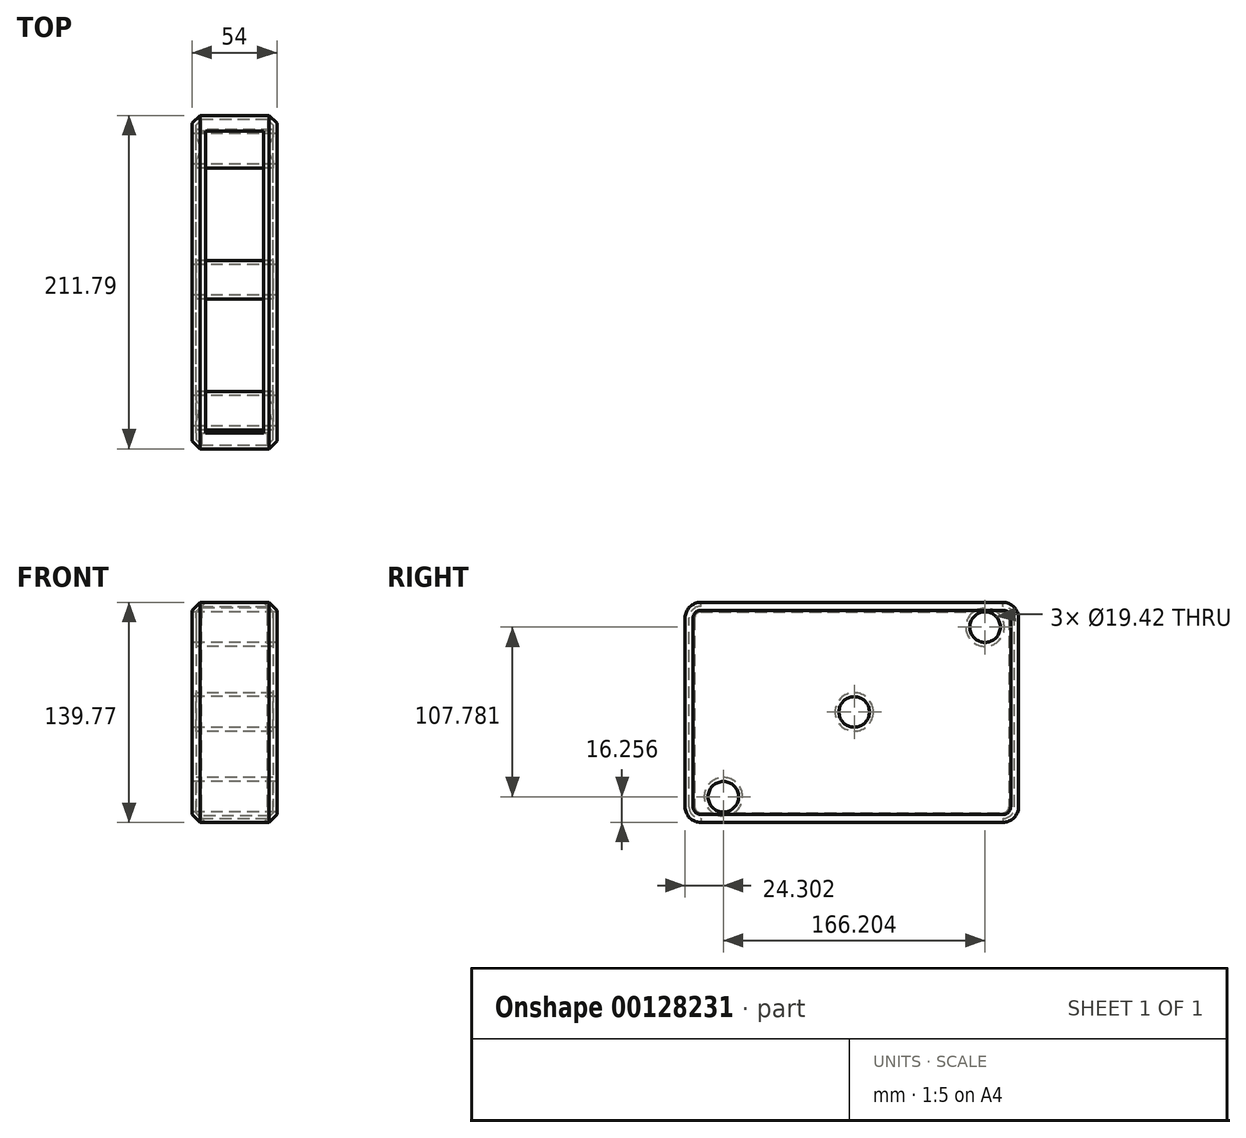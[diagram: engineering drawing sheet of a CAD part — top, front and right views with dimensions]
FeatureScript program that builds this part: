
annotation { "Feature Type Name" : "Feature", "Feature Type Description" : "" }
export const myFeature = defineFeature(function(context is Context, id is Id, definition is map)
    precondition{}
    {
        {
            var Q0;
            Q0=qCreatedBy(makeId("Right.planeOp"),FACE);
            var sketch = newSketch(context, id + "F0", { "sketchPlane" : qUnion([Q0])});
            skLineSegment(sketch, "E0.bottom", {"start": v(-68.29, 56.83) * mm, "end": v(143.5, 56.83) * mm});
            skLineSegment(sketch, "E0.top", {"start": v(-68.29, -82.94) * mm, "end": v(143.5, -82.94) * mm});
            skLineSegment(sketch, "E0.left", {"start": v(-68.29, 56.83) * mm, "end": v(-68.29, -82.94) * mm});
            skLineSegment(sketch, "E0.right", {"start": v(143.5, 56.83) * mm, "end": v(143.5, -82.94) * mm});
            skCircle(sketch, "E1", {"center": v(122.22, 41.1) * mm, "radius": 9.7 * mm});
            skCircle(sketch, "E2.1.0.0", {"center": v(39.11, -12.8) * mm, "radius": 9.7 * mm});
            skCircle(sketch, "E2.2.0.0", {"center": v(-43.99, -66.68) * mm, "radius": 9.7 * mm});
            skLineSegment(sketch, "E2.direction1", {"start": v(122.22, 41.1) * mm, "end": v(39.11, -12.8) * mm, "construction": true});
            skSolve(sketch);
        }
        {
            var Q0;
            Q0=makeQuery(id+"F0.imprint","IMPRINT",FACE,{"disambiguationData":[TD([[makeQuery(id+"F0.imprint","IMPRINT",EDGE,{"derivedFrom":sQuery(id+"F0.wireOp",EDGE,"E0.bottom")}),-1.0]])]});
            extrude(context, id + "F1", {"entities" : qUnion([Q0]), "depth" : 54 * mm});
        }
        {
            var Q0;
            Q0=makeQuery(id+"F1.opExtrude","SWEPT_EDGE",EDGE,{"disambiguationData":[OSD([sQuery(id+"F0.wireOp",EDGE,"E0.bottom"),sQuery(id+"F0.wireOp",EDGE,"E0.right")])]});
            var Q1;
            Q1=makeQuery(id+"F1.opExtrude","SWEPT_EDGE",EDGE,{"disambiguationData":[OSD([sQuery(id+"F0.wireOp",EDGE,"E0.top"),sQuery(id+"F0.wireOp",EDGE,"E0.left")])]});
            var Q2;
            Q2=makeQuery(id+"F1.opExtrude","SWEPT_EDGE",EDGE,{"disambiguationData":[OSD([sQuery(id+"F0.wireOp",EDGE,"E0.bottom"),sQuery(id+"F0.wireOp",EDGE,"E0.left")])]});
            var Q3;
            Q3=makeQuery(id+"F1.opExtrude","SWEPT_EDGE",EDGE,{"disambiguationData":[OSD([sQuery(id+"F0.wireOp",EDGE,"E0.top"),sQuery(id+"F0.wireOp",EDGE,"E0.right")])]});
            fillet(context, id + "F2", {"entities" : qUnion([Q0, Q1, Q2, Q3]), "radius" : 10 * mm, "tangentPropagation" : true, "allowEdgeOverflow" : false});
        }
        {
            var Q0;
            Q0=makeQuery(id+"F1.opExtrude","CAP_EDGE",EDGE,{"disambiguationData":[OSD([sQuery(id+"F0.wireOp",EDGE,"E0.top")])],"isStart":false});
            chamfer(context, id + "F3", {"entities" : qUnion([Q0]), "width" : 5 * mm, "tangentPropagation" : true});
        }
        {
            var Q0;
            Q0=makeQuery(id+"F1.opExtrude","CAP_EDGE",EDGE,{"disambiguationData":[OSD([sQuery(id+"F0.wireOp",EDGE,"E0.top")])],"isStart":true});
            chamfer(context, id + "F4", {"entities" : qUnion([Q0]), "width" : 5 * mm, "tangentPropagation" : true});
        }
        {
            var Q0;
            Q0=makeQuery(id+"F1.opExtrude","SWEPT_FACE",FACE,{"disambiguationData":[OSD([sQuery(id+"F0.wireOp",EDGE,"E0.bottom")])]});
            var Q1;
            Q1=makeQuery(id+"F1.opExtrude","SWEPT_FACE",FACE,{"disambiguationData":[OSD([sQuery(id+"F0.wireOp",EDGE,"E0.top")])]});
            shell(context, id + "F5", {"entities" : qUnion([Q0, Q1]), "thickness" : 2.5 * mm});
        }
    });
